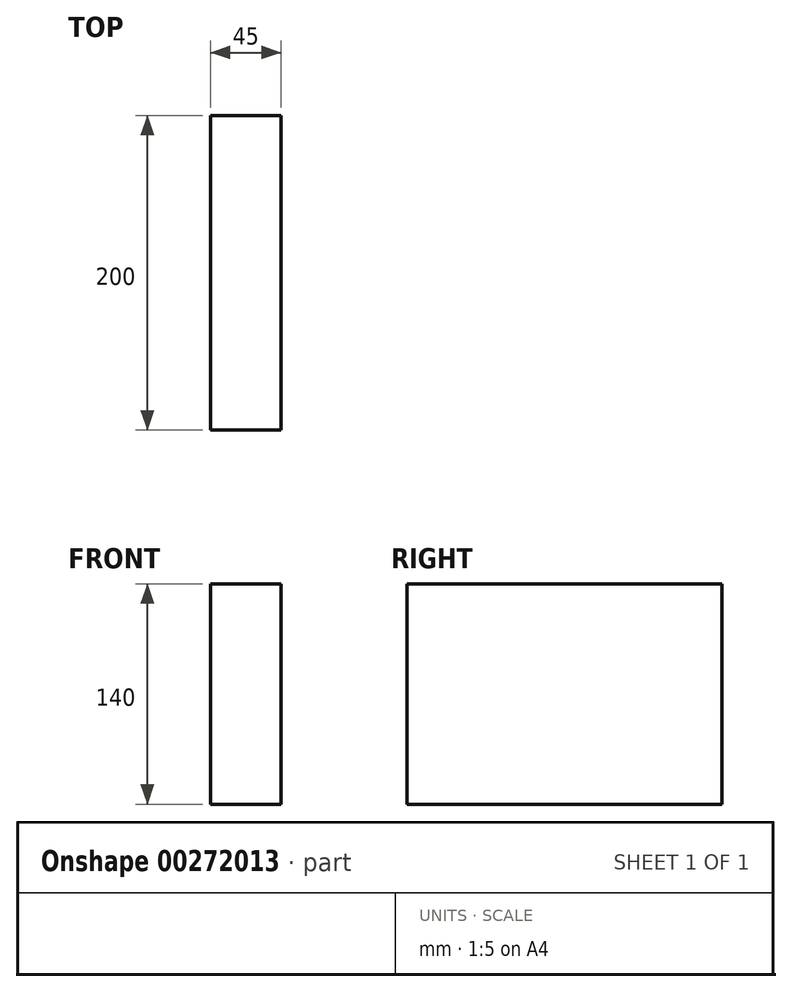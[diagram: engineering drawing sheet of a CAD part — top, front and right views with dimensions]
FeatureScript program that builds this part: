
annotation { "Feature Type Name" : "Feature", "Feature Type Description" : "" }
export const myFeature = defineFeature(function(context is Context, id is Id, definition is map)
    precondition{}
    {
        {
            var Q0;
            Q0=qCreatedBy(makeId("Front.planeOp"),FACE);
            var sketch = newSketch(context, id + "F0", { "sketchPlane" : qUnion([Q0])});
            skLineSegment(sketch, "E0.bottom", {"start": v(0, 0) * mm, "end": v(-45, 0) * mm});
            skLineSegment(sketch, "E0.top", {"start": v(0, -140) * mm, "end": v(-45, -140) * mm});
            skLineSegment(sketch, "E0.left", {"start": v(0, 0) * mm, "end": v(0, -140) * mm});
            skLineSegment(sketch, "E0.right", {"start": v(-45, 0) * mm, "end": v(-45, -140) * mm});
            skSolve(sketch);
        }
        {
            var Q0;
            Q0=makeQuery(id+"F0.imprint","IMPRINT",FACE,{"disambiguationData":[TD([[makeQuery(id+"F0.imprint","IMPRINT",EDGE,{"derivedFrom":sQuery(id+"F0.wireOp",EDGE,"E0.bottom")}),1.0]])]});
            extrude(context, id + "F1", {"entities" : qUnion([Q0]), "oppositeDirection" : true, "depth" : 200 * mm});
        }
    });
